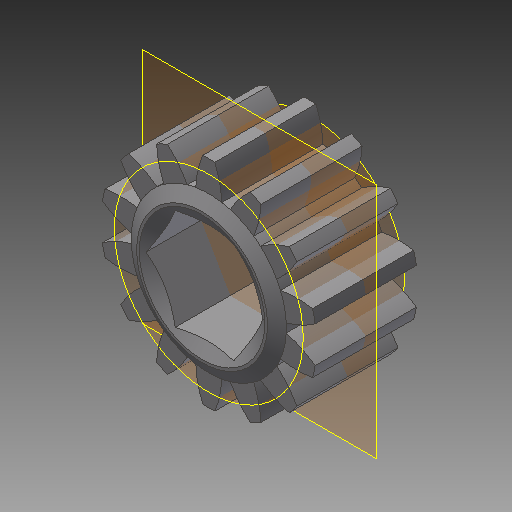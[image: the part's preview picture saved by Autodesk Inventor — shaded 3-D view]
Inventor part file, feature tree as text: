
AUTODESK INVENTOR PART (.ipt)
format: ipt  version: 2018 (Build 220112000, 112)  size: 221,184 bytes
history: native  units: in
note: dims shown in document units (in); Inventor stores cm internally (conversion verified against a paired STEP export)
features: other x3, plane x1, imported_body x1, sketch x1, extrude x1
ambient origin geometry x8: Origin, YZ Plane, XZ Plane, XY Plane, X Axis, Y Axis, Z Axis, Center Point
bodies: Body1 (feature_tree), Body2 (feature_tree)
feature tree (7):
  other  "Toughbox_d08"
  other  "SW-GEAR-20DP-14T.ipt1"
  plane  "Work Plane MID-TOOTH"
  imported_body  "Base1"
  sketch  "Sketch1"  dims[d0=0.7in d1=0.3937in d2=0.0in]
  other  "Srf PITCH CIRCLE"
  extrude  "ExtrusionSrf1"  Depth=0.3937in TaperAngle=0.0deg
